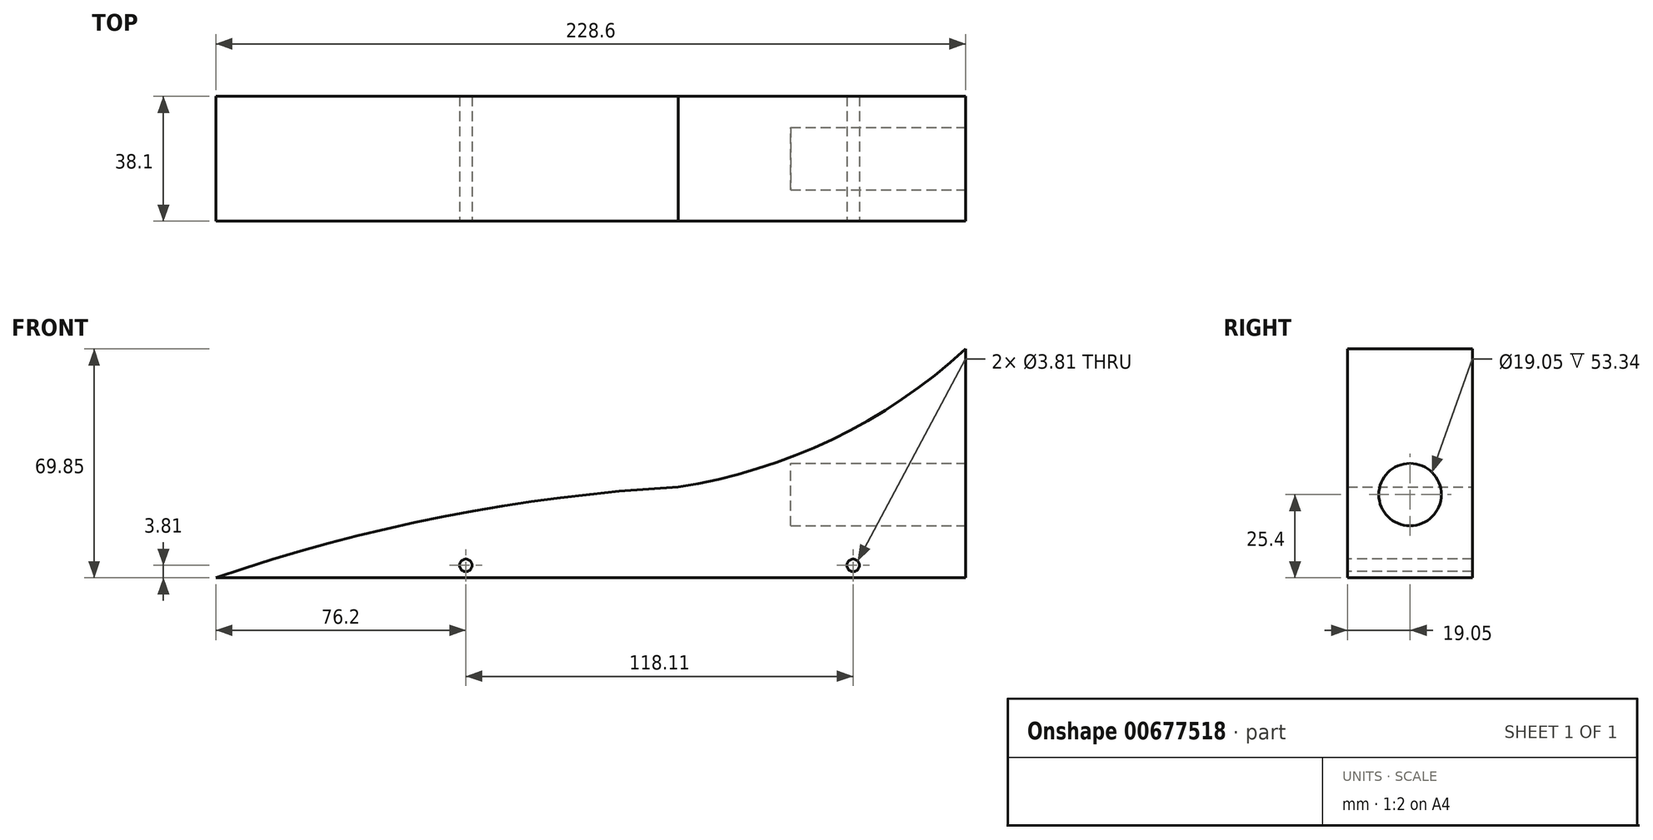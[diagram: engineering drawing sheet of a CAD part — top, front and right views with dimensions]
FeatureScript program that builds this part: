
annotation { "Feature Type Name" : "Feature", "Feature Type Description" : "" }
export const myFeature = defineFeature(function(context is Context, id is Id, definition is map)
    precondition{}
    {
        {
            var Q0;
            Q0=qCreatedBy(makeId("Front.planeOp"),FACE);
            var sketch = newSketch(context, id + "F0", { "sketchPlane" : qUnion([Q0])});
            skLineSegment(sketch, "E0", {"start": v(0, 0) * mm, "end": v(228.6, 0) * mm});
            skLineSegment(sketch, "E1", {"start": v(228.6, 0) * mm, "end": v(228.6, 25.4) * mm});
            skArc(sketch, "E2", {"start": v(228.6, 25.4) * mm, "mid": v(112.9, 25.37) * mm, "end": v(0, 0) * mm});
            skLineSegment(sketch, "E3", {"start": v(228.6, 0) * mm, "end": v(228.6, 69.85) * mm});
            skArc(sketch, "E4", {"start": v(140.95, 27.73) * mm, "mid": v(187.92, 42.25) * mm, "end": v(228.6, 69.85) * mm});
            skSolve(sketch);
        }
        {
            var Q0;
            {var subQ0=sQuery(id+"F0.wireOp",EDGE,"E0");Q0=makeQuery(id+"F0.imprint","IMPRINT",FACE,{"disambiguationData":[TD([[makeQuery(id+"F0.imprint","IMPRINT",EDGE,{"derivedFrom":subQ0}),1.0]])]});}
            var Q1;
            {var subQ0=sQuery(id+"F0.wireOp",EDGE,"iLzQDKXy-x8WK-pVnt-5sL7-5Lv4gVgy8G4H");Q1=makeQuery(id+"F0.imprint","IMPRINT",FACE,{"disambiguationData":[TD([[makeQuery(id+"F0.imprint","IMPRINT",EDGE,{"derivedFrom":subQ0}),1.0]])]});}
            extrude(context, id + "F1", {"entities" : qUnion([Q0, Q1]), "depth" : 38.1 * mm, "offsetDistance" : 25.4 * mm});
        }
        {
            var Q0;
            Q0=makeQuery(id+"F1.opExtrude","CAP_EDGE",EDGE,{"disambiguationData":[OSD([sQuery(id+"F0.wireOp",EDGE,"CIHMKfAh-2RKG-jgX9-hOFv-mB7a5E6RXKQq")])],"isStart":true});
            var Q1;
            Q1=makeQuery(id+"F1.opExtrude","CAP_EDGE",EDGE,{"disambiguationData":[OSD([sQuery(id+"F0.wireOp",EDGE,"E2")])],"isStart":true});
            var Q2;
            Q2=makeQuery(id+"F1.opExtrude","CAP_EDGE",EDGE,{"disambiguationData":[OSD([sQuery(id+"F0.wireOp",EDGE,"E2")])],"isStart":false});
            var Q3;
            Q3=makeQuery(id+"F1.opExtrude","CAP_EDGE",EDGE,{"disambiguationData":[OSD([sQuery(id+"F0.wireOp",EDGE,"CIHMKfAh-2RKG-jgX9-hOFv-mB7a5E6RXKQq")])],"isStart":false});
            fillet(context, id + "F2", {"entities" : qUnion([Q0, Q1, Q2, Q3]), "radius" : 5.08 * mm, "tangentPropagation" : true, "allowEdgeOverflow" : false});
        }
        {
            var Q0;
            Q0 = qSketchRegion(id + "F0", true);
            extrude(context, id + "F3", {"entities" : qUnion([Q0]), "operationType" : NewBodyOperationType.ADD, "depth" : 38.1 * mm, "offsetDistance" : 25.4 * mm});
        }
        {
            var Q0;
            {var subQ0=sQuery(id+"F0.wireOp",EDGE,"E3");Q0=makeQuery(id+"F3.boolean.opBoolean","MERGE",FACE,{"derivedFrom":[makeQuery(id+"F1.opExtrude","SWEPT_FACE",FACE,{"disambiguationData":[OSD([subQ0])]}),makeQuery(id+"F3.opExtrude","SWEPT_FACE",FACE,{"disambiguationData":[OSD([subQ0])]})]});}
            var sketch = newSketch(context, id + "F4", { "sketchPlane" : qUnion([Q0])});
            skCircle(sketch, "E5", {"center": v(-19.05, 25.4) * mm, "radius": 9.53 * mm});
            skSolve(sketch);
        }
        {
            var Q0;
            Q0=makeQuery(id+"F4.imprint","IMPRINT",FACE,{"disambiguationData":[TD([[makeQuery(id+"F4.imprint","IMPRINT",EDGE,{"derivedFrom":sQuery(id+"F4.wireOp",EDGE,"E5")}),1.0]])]});
            extrude(context, id + "F5", {"entities" : qUnion([Q0]), "operationType" : NewBodyOperationType.REMOVE, "oppositeDirection" : true, "depth" : 53.34 * mm, "offsetDistance" : 25.4 * mm});
        }
        {
            var Q0;
            {var subQ0=sQuery(id+"F0.wireOp",EDGE,"E3");var subQ1=sQuery(id+"F0.wireOp",EDGE,"E2");var subQ2=sQuery(id+"F0.wireOp",EDGE,"E0");Q0=makeQuery(id+"F3.boolean.opBoolean","MERGE",FACE,{"derivedFrom":[makeQuery(id+"F1.opExtrude","CAP_FACE",FACE,{"disambiguationData":[OSD([subQ2,subQ1,subQ0])],"isStart":false}),makeQuery(id+"F3.opExtrude","CAP_FACE",FACE,{"disambiguationData":[OSD([subQ2,subQ1,subQ0,sQuery(id+"F0.wireOp",EDGE,"E4")])],"isStart":false})]});}
            var sketch = newSketch(context, id + "F6", { "sketchPlane" : qUnion([Q0])});
            skLineSegment(sketch, "E6", {"start": v(0, 0) * mm, "end": v(76.2, 0) * mm});
            skCircle(sketch, "E7", {"center": v(76.2, 3.81) * mm, "radius": 1.9 * mm});
            skCircle(sketch, "E8", {"center": v(194.3, 3.81) * mm, "radius": 1.9 * mm});
            skSolve(sketch);
        }
        {
            var Q0;
            Q0=makeQuery(id+"F6.imprint","IMPRINT",FACE,{"disambiguationData":[TD([[makeQuery(id+"F6.imprint","IMPRINT",EDGE,{"derivedFrom":sQuery(id+"F6.wireOp",EDGE,"E7")}),1.0]])]});
            extrude(context, id + "F7", {"entities" : qUnion([Q0]), "operationType" : NewBodyOperationType.REMOVE, "endBound" : BoundingType.THROUGH_ALL, "oppositeDirection" : true, "depth" : 25.4 * mm, "offsetDistance" : 25.4 * mm});
        }
        {
            var Q0;
            Q0=makeQuery(id+"F6.imprint","IMPRINT",FACE,{"disambiguationData":[TD([[makeQuery(id+"F6.imprint","IMPRINT",EDGE,{"derivedFrom":sQuery(id+"F6.wireOp",EDGE,"E8")}),1.0]])]});
            extrude(context, id + "F8", {"entities" : qUnion([Q0]), "operationType" : NewBodyOperationType.REMOVE, "endBound" : BoundingType.THROUGH_ALL, "oppositeDirection" : true, "depth" : 25.4 * mm, "offsetDistance" : 25.4 * mm});
        }
    });
